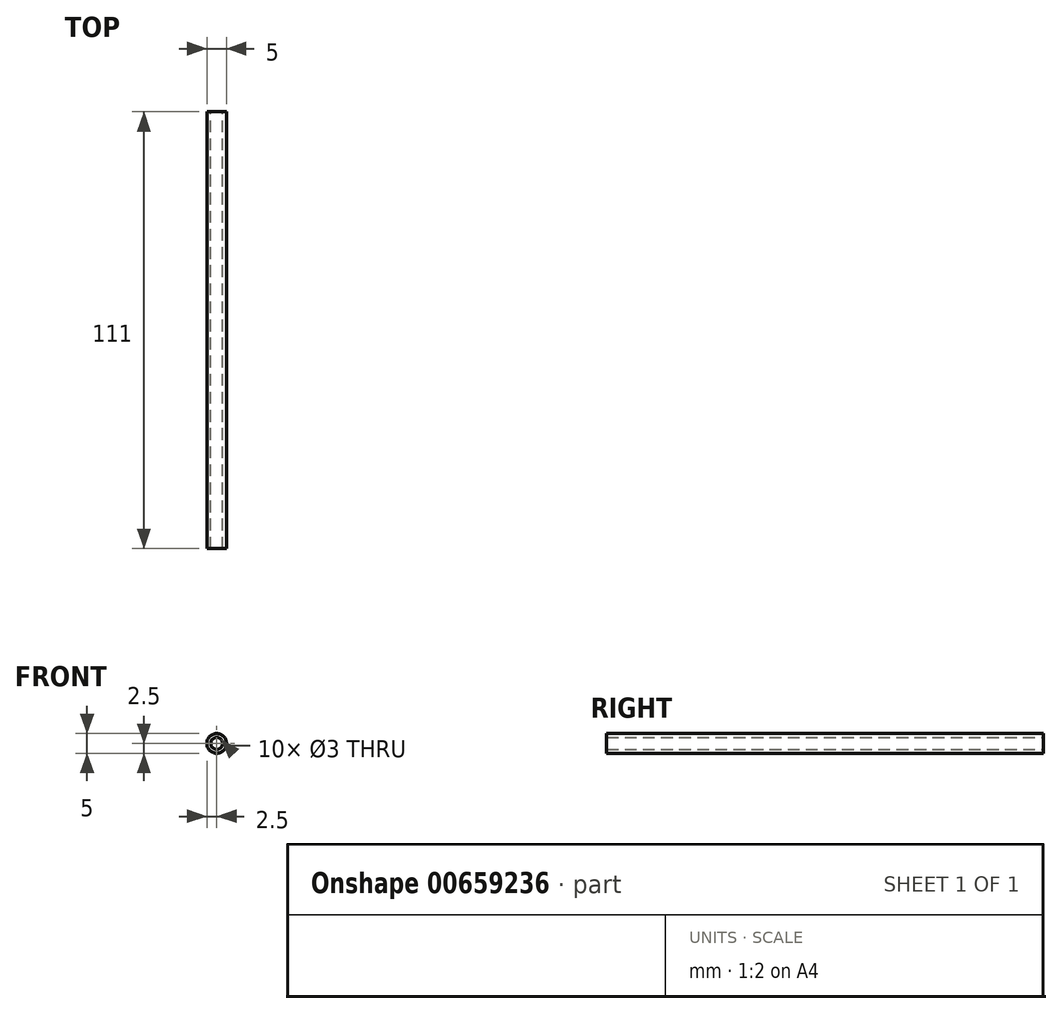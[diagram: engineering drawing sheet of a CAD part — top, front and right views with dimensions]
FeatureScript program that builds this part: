
annotation { "Feature Type Name" : "Feature", "Feature Type Description" : "" }
export const myFeature = defineFeature(function(context is Context, id is Id, definition is map)
    precondition{}
    {
        {
            var Q0;
            Q0=qCreatedBy(makeId("Front.planeOp"),FACE);
            var sketch = newSketch(context, id + "F0", { "sketchPlane" : qUnion([Q0])});
            skCircle(sketch, "E0", {"center": v(0, 0) * mm, "radius": 2.5 * mm});
            skCircle(sketch, "E1", {"center": v(0, 0) * mm, "radius": 1.5 * mm});
            skSolve(sketch);
        }
        {
            var Q0;
            Q0=makeQuery(id+"F0.imprint","IMPRINT",FACE,{"disambiguationData":[TD([[makeQuery(id+"F0.imprint","IMPRINT",EDGE,{"derivedFrom":sQuery(id+"F0.wireOp",EDGE,"E0")}),1.0]])]});
            extrude(context, id + "F1", {"entities" : qUnion([Q0]), "depth" : 111 * mm, "offsetDistance" : 25 * mm, "symmetric" : true});
        }
    });
